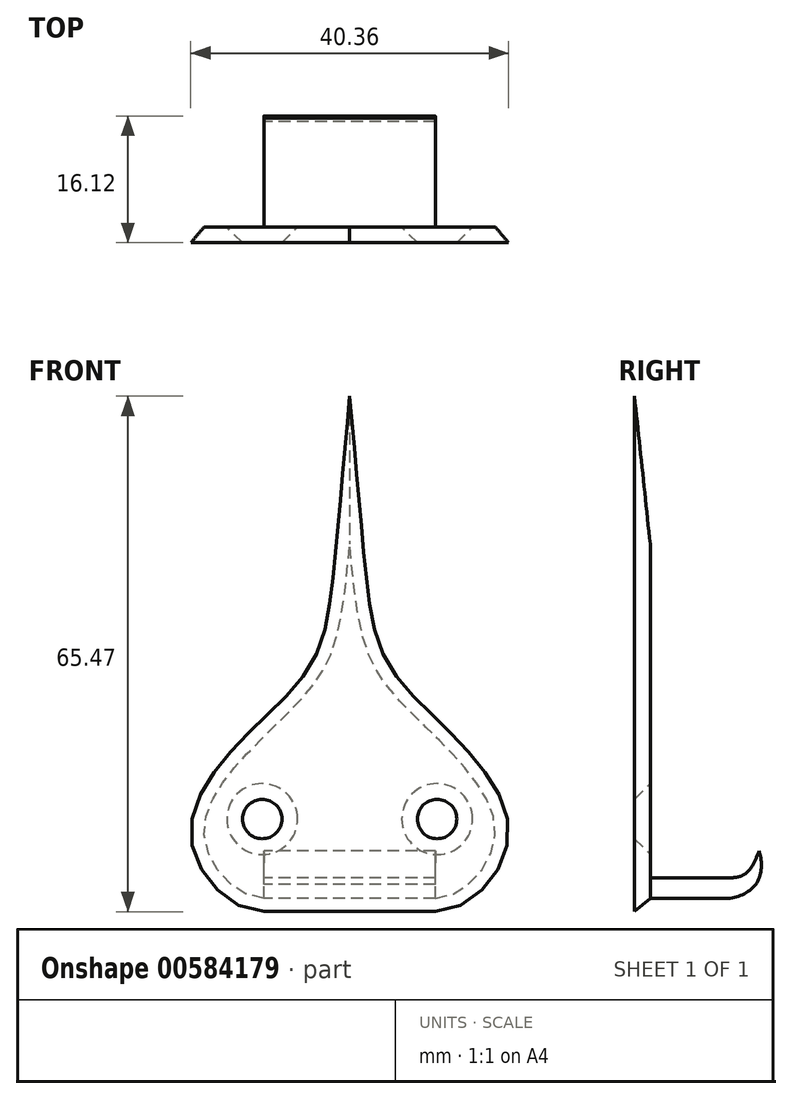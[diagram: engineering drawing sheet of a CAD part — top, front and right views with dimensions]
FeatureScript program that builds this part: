
annotation { "Feature Type Name" : "Feature", "Feature Type Description" : "" }
export const myFeature = defineFeature(function(context is Context, id is Id, definition is map)
    precondition{}
    {
        {
            var Q0;
            Q0=qCreatedBy(makeId("Front.planeOp"),FACE);
            var sketch = newSketch(context, id + "F0", { "sketchPlane" : qUnion([Q0])});
            skFitSpline(sketch, "E0", {"points": [v(-10.9, 0) * mm, v(-18.5, 8.65) * mm, v(-6.22, 25.25) * mm, v(0, 45) * mm], "startDerivative": vector(-37.87, 0) * mm, "endDerivative": vector(8.6, 95.92) * mm});
            skFitSpline(sketch, "E1", {"points": [v(10.9, 0) * mm, v(18.5, 8.65) * mm, v(6.22, 25.25) * mm, v(0, 45) * mm], "startDerivative": vector(37.87, 0) * mm, "endDerivative": vector(-8.6, 95.92) * mm});
            skLineSegment(sketch, "E2", {"start": v(-10.9, 0) * mm, "end": v(10.9, 0) * mm});
            skSolve(sketch);
        }
        {
            var Q0;
            Q0=makeQuery(id+"F0.imprint","IMPRINT",FACE,{"disambiguationData":[TD([[makeQuery(id+"F0.imprint","IMPRINT",EDGE,{"derivedFrom":sQuery(id+"F0.wireOp",EDGE,"E0")}),-1.0]])]});
            extrude(context, id + "F1", {"entities" : qUnion([Q0]), "depth" : 2 * mm, "offsetDistance" : 25 * mm, "hasDraft" : true, "draftAngle" : 40 * degree});
        }
        {
            var Q0;
            Q0=makeQuery(id+"F1.opExtrude","CAP_FACE",FACE,{"disambiguationData":[OSD([sQuery(id+"F0.wireOp",EDGE,"E0"),sQuery(id+"F0.wireOp",EDGE,"E1"),sQuery(id+"F0.wireOp",EDGE,"E2")])],"isStart":true});
            var sketch = newSketch(context, id + "F2", { "sketchPlane" : qUnion([Q0])});
            skLineSegment(sketch, "E3.bottom", {"start": v(-10.9, 0) * mm, "end": v(10.9, 0) * mm});
            skLineSegment(sketch, "E3.top", {"start": v(-10.9, 2.64) * mm, "end": v(10.9, 2.64) * mm});
            skLineSegment(sketch, "E3.left", {"start": v(-10.9, 0) * mm, "end": v(-10.9, 2.64) * mm});
            skLineSegment(sketch, "E3.right", {"start": v(10.9, 0) * mm, "end": v(10.9, 2.64) * mm});
            skLineSegment(sketch, "E4", {"start": v(-16.67, 11.32) * mm, "end": v(16.2, 11.32) * mm, "construction": true});
            skSolve(sketch);
        }
        {
            var Q0;
            Q0=makeQuery(id+"F2.imprint","IMPRINT",FACE,{"disambiguationData":[TD([[makeQuery(id+"F2.imprint","IMPRINT",EDGE,{"derivedFrom":sQuery(id+"F2.wireOp",EDGE,"E3.bottom")}),-1.0]])]});
            var Q1;
            Q1=sQuery(id+"F2.wireOp",EDGE,"E3.top");
            extrude(context, id + "F3", {"entities" : qUnion([Q0]), "operationType" : NewBodyOperationType.ADD, "surfaceEntities" : qUnion([Q1]), "depth" : 12 * mm, "offsetDistance" : 25 * mm});
        }
        {
            var Q0;
            Q0=makeQuery(id+"F3.opExtrude","CAP_FACE",FACE,{"disambiguationData":[OSD([sQuery(id+"F2.wireOp",EDGE,"E3.bottom"),sQuery(id+"F2.wireOp",EDGE,"E3.top"),sQuery(id+"F2.wireOp",EDGE,"E3.left"),sQuery(id+"F2.wireOp",EDGE,"E3.right")])],"isStart":false});
            var Q1;
            Q1=sQuery(id+"F2.wireOp",EDGE,"E4");
            revolve(context, id + "F4", {"operationType" : NewBodyOperationType.ADD, "entities" : qUnion([Q0]), "axis" : qUnion([Q1]), "revolveType" : RevolveType.ONE_DIRECTION, "oppositeDirection" : true, "angle" : 15 * degree});
        }
        {
            var Q0;
            Q0=makeQuery(id+"F2.imprint","IMPRINT",FACE,{"disambiguationData":[TD([[makeQuery(id+"F2.imprint","IMPRINT",EDGE,{"derivedFrom":sQuery(id+"F2.wireOp",EDGE,"E3.top")}),1.0]])]});
            var sketch = newSketch(context, id + "F5", { "sketchPlane" : qUnion([Q0])});
            skPoint(sketch, "E5", {"position": v(-11.1, 10.08) * mm});
            skPoint(sketch, "E6", {"position": v(11.1, 10.08) * mm});
            skSolve(sketch);
        }
        {
            var Q0;
            Q0=sQuery(id+"F5.wireOp",VERTEX,"E5");
            var Q1;
            Q1=sQuery(id+"F5.wireOp",VERTEX,"E6");
            var Q2;
            Q2=makeQuery(id+"F1.opExtrude","SWEPT_BODY",BODY,{"disambiguationData":[OSD([sQuery(id+"F0.wireOp",EDGE,"E0"),sQuery(id+"F0.wireOp",EDGE,"E1"),sQuery(id+"F0.wireOp",EDGE,"E2")])]});
            hole(context, id + "F6", {"style" : HoleStyle.C_SINK, "endStyle" : HoleEndStyle.THROUGH, "holeDiameter" : 4 * mm, "cSinkDiameter" : 9 * mm, "cSinkAngle" : 90 * degree, "majorDiameter" : 5 * mm, "isTappedThrough" : true, "tappedDepth" : 12 * mm, "tapClearance" : 3, "locations" : qUnion([Q0, Q1]), "scope" : qUnion([Q2])});
        }
        {
            var Q0;
            Q0=makeQuery(id+"F4.opRevolve","CAP_EDGE",EDGE,{"disambiguationData":[OSD([sQuery(id+"F2.wireOp",EDGE,"E3.bottom")]),OD(1.0)],"isStart":false});
            var Q1;
            {var subQ0=sQuery(id+"F2.wireOp",EDGE,"E3.bottom");Q1=makeQuery(id+"F4.boolean.opBoolean","MERGE",EDGE,{"derivedFrom":[makeQuery(id+"F3.opExtrude","CAP_EDGE",EDGE,{"disambiguationData":[OSD([subQ0])],"isStart":false}),makeQuery(id+"F4.opRevolve","CAP_EDGE",EDGE,{"disambiguationData":[OSD([subQ0]),OD(0.0)],"isStart":false})]});}
            fillet(context, id + "F7", {"entities" : qUnion([Q0, Q1]), "radius" : 5 * mm, "tangentPropagation" : true, "allowEdgeOverflow" : false});
        }
        {
            var Q0;
            {var subQ0=sQuery(id+"F2.wireOp",EDGE,"E3.top");Q0=makeQuery(id+"F4.boolean.opBoolean","MERGE",EDGE,{"derivedFrom":[makeQuery(id+"F3.opExtrude","CAP_EDGE",EDGE,{"disambiguationData":[OSD([subQ0])],"isStart":false}),makeQuery(id+"F4.opRevolve","CAP_EDGE",EDGE,{"disambiguationData":[OSD([subQ0]),OD(0.0)],"isStart":false})]});}
            chamfer(context, id + "F8", {"entities" : qUnion([Q0]), "width" : 1.5 * mm, "tangentPropagation" : true});
        }
        {
            var Q0;
            {var subQ0=sQuery(id+"F2.wireOp",EDGE,"E3.top");Q0=makeQuery(id+"F8.opChamfer","BLEND_EDGE",EDGE,{"blendedFrom":[makeQuery(id+"F4.boolean.opBoolean","MERGE",EDGE,{"derivedFrom":[makeQuery(id+"F3.opExtrude","CAP_EDGE",EDGE,{"disambiguationData":[OSD([subQ0])],"isStart":false}),makeQuery(id+"F4.opRevolve","CAP_EDGE",EDGE,{"disambiguationData":[OSD([subQ0]),OD(0.0)],"isStart":false})]}),makeQuery(id+"F3.opExtrude","SWEPT_FACE",FACE,{"disambiguationData":[OSD([subQ0])]})],"blendedInto":[makeQuery(id+"F3.opExtrude","SWEPT_FACE",FACE,{"disambiguationData":[OSD([subQ0])]})]});}
            var Q1;
            {var subQ0=sQuery(id+"F2.wireOp",EDGE,"E3.top");Q1=makeQuery(id+"F8.opChamfer","BLEND_EDGE",EDGE,{"blendedFrom":[makeQuery(id+"F4.boolean.opBoolean","MERGE",EDGE,{"derivedFrom":[makeQuery(id+"F3.opExtrude","CAP_EDGE",EDGE,{"disambiguationData":[OSD([subQ0])],"isStart":false}),makeQuery(id+"F4.opRevolve","CAP_EDGE",EDGE,{"disambiguationData":[OSD([subQ0]),OD(0.0)],"isStart":false})]}),makeQuery(id+"F4.opRevolve","SWEPT_FACE",FACE,{"disambiguationData":[OSD([subQ0])]})],"blendedInto":[makeQuery(id+"F4.opRevolve","SWEPT_FACE",FACE,{"disambiguationData":[OSD([subQ0])]})]});}
            fillet(context, id + "F9", {"entities" : qUnion([Q0, Q1]), "radius" : 2.67 * mm, "tangentPropagation" : true, "allowEdgeOverflow" : false});
        }
    });
